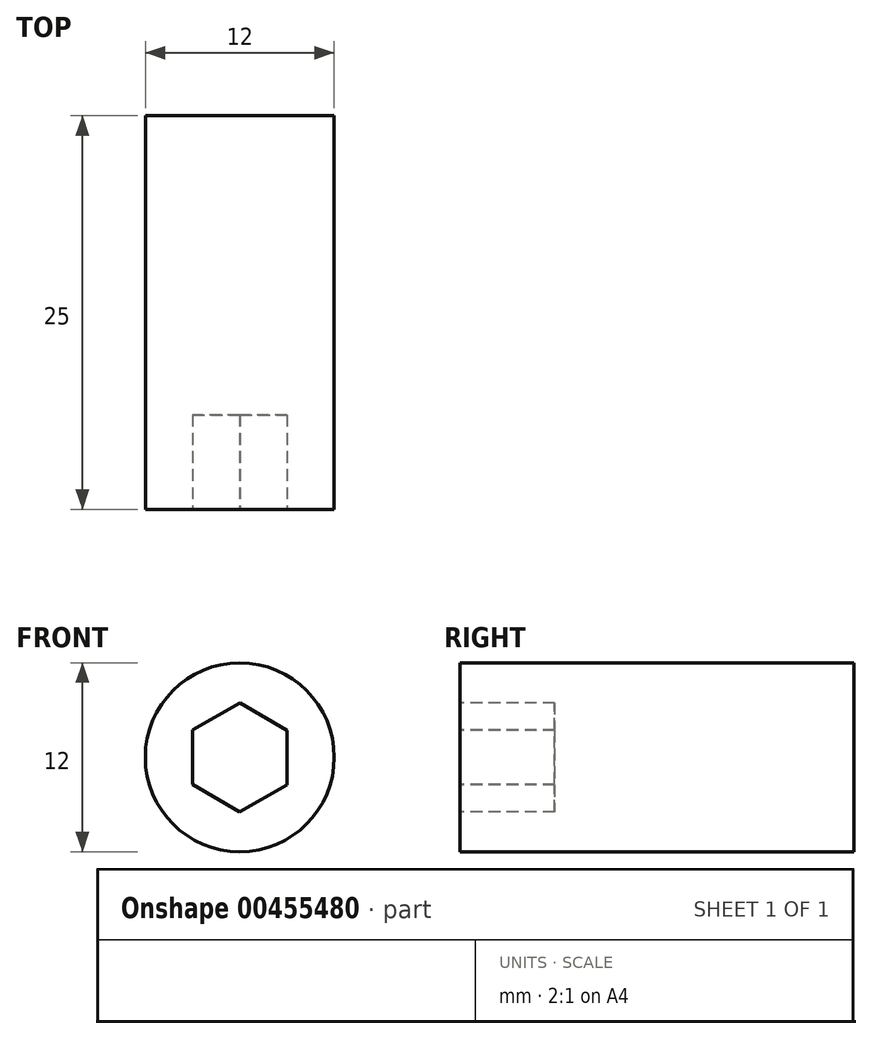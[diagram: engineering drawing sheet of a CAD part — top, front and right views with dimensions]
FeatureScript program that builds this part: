
annotation { "Feature Type Name" : "Feature", "Feature Type Description" : "" }
export const myFeature = defineFeature(function(context is Context, id is Id, definition is map)
    precondition{}
    {
        {
            var Q0;
            Q0=qCreatedBy(makeId("Front.planeOp"),FACE);
            var sketch = newSketch(context, id + "F0", { "sketchPlane" : qUnion([Q0])});
            skCircle(sketch, "E0", {"center": v(0, 0) * mm, "radius": 6 * mm});
            skSolve(sketch);
        }
        {
            var Q0;
            Q0 = qSketchRegion(id + "F0", true);
            extrude(context, id + "F1", {"entities" : qUnion([Q0]), "oppositeDirection" : true, "depth" : 25 * mm});
        }
        {
            var Q0;
            Q0=makeQuery(id+"F1.opExtrude","CAP_FACE",FACE,{"disambiguationData":[OSD([sQuery(id+"F0.wireOp",EDGE,"E0")])],"isStart":true});
            var sketch = newSketch(context, id + "F2", { "sketchPlane" : qUnion([Q0])});
            skLineSegment(sketch, "E1.0", {"start": v(-2.99, 1.75) * mm, "end": v(0.02, 3.46) * mm});
            skLineSegment(sketch, "E1.1", {"start": v(0.02, 3.46) * mm, "end": v(3.01, 1.71) * mm});
            skLineSegment(sketch, "E1.2", {"start": v(3.01, 1.71) * mm, "end": v(2.99, -1.75) * mm});
            skLineSegment(sketch, "E1.3", {"start": v(2.99, -1.75) * mm, "end": v(-0.02, -3.46) * mm});
            skLineSegment(sketch, "E1.4", {"start": v(-0.02, -3.46) * mm, "end": v(-3.01, -1.71) * mm});
            skLineSegment(sketch, "E1.5", {"start": v(-3.01, -1.71) * mm, "end": v(-2.99, 1.75) * mm});
            skPoint(sketch, "E1.0.midPoint", {"position": v(-1.48, 2.6) * mm});
            skSolve(sketch);
        }
        {
            var Q0;
            Q0 = qSketchRegion(id + "F2", true);
            extrude(context, id + "F3", {"entities" : qUnion([Q0]), "operationType" : NewBodyOperationType.REMOVE, "oppositeDirection" : true, "depth" : 6 * mm});
        }
    });
